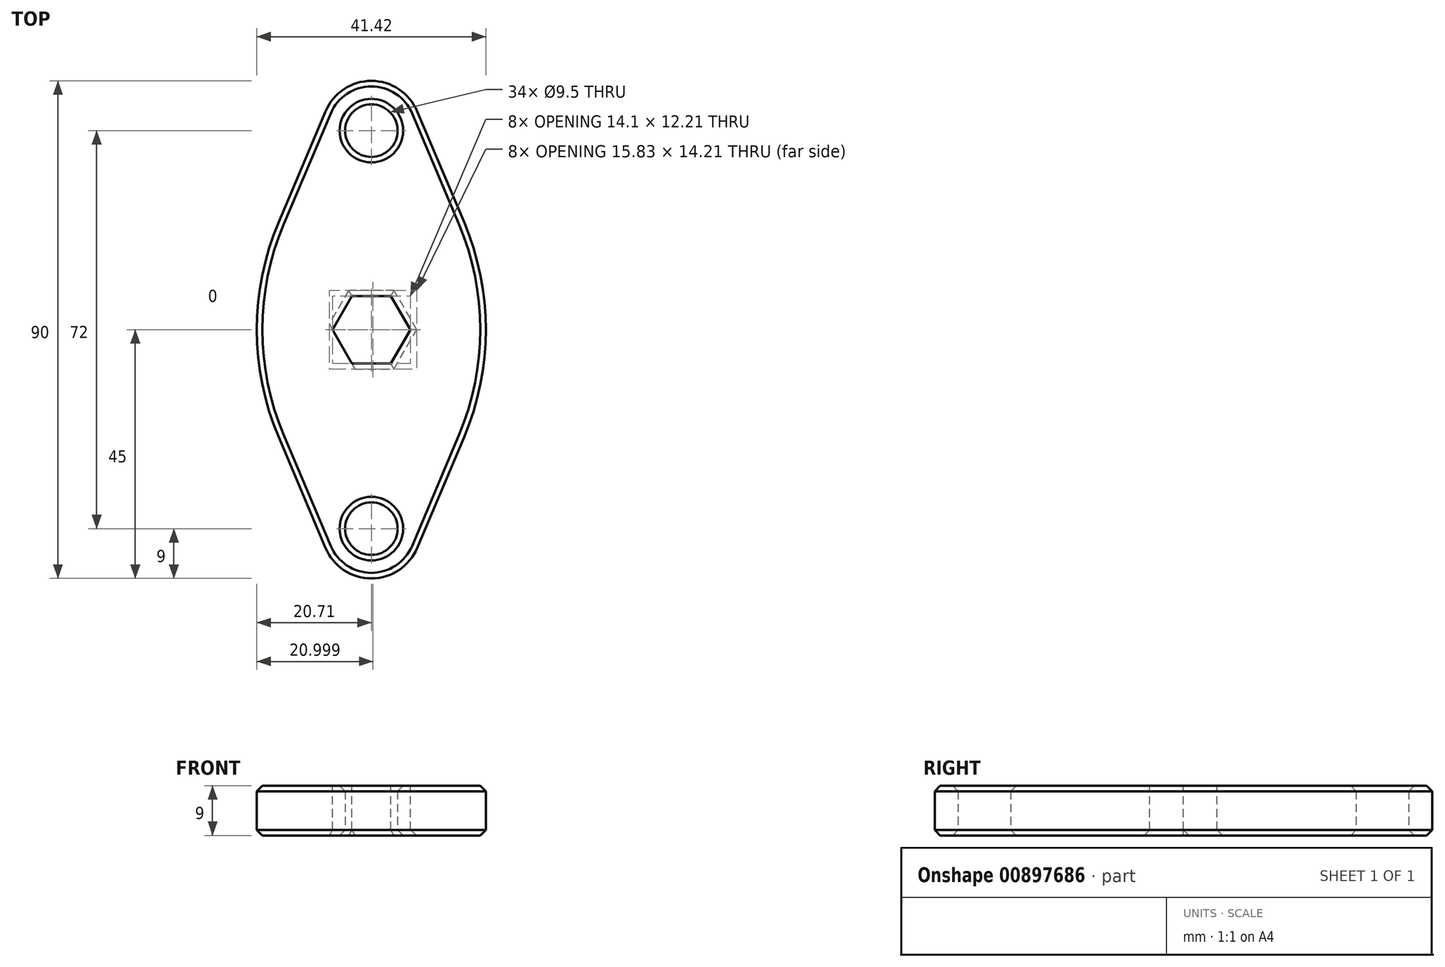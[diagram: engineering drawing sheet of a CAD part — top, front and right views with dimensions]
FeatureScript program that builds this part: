
annotation { "Feature Type Name" : "Feature", "Feature Type Description" : "" }
export const myFeature = defineFeature(function(context is Context, id is Id, definition is map)
    precondition{}
    {
        {
            var Q0;
            Q0=qCreatedBy(makeId("Top.planeOp"),FACE);
            var sketch = newSketch(context, id + "F0", { "sketchPlane" : qUnion([Q0])});
            skLineSegment(sketch, "E0", {"start": v(0, 83.57) * mm, "end": v(0, -89.6) * mm, "construction": true});
            skLineSegment(sketch, "E1", {"start": v(81.05, 0) * mm, "end": v(-79.37, 0) * mm, "construction": true});
            skArc(sketch, "E2", {"start": v(8.29, 39.5) * mm, "mid": v(0, 45) * mm, "end": v(-8.29, 39.5) * mm});
            skLineSegment(sketch, "E3", {"start": v(-26.39, 36) * mm, "end": v(35.06, 36) * mm, "construction": true});
            skArc(sketch, "E4.MirrorCS", {"start": v(8.29, -39.5) * mm, "mid": v(0, -45) * mm, "end": v(-8.29, -39.5) * mm});
            skLineSegment(sketch, "E5", {"start": v(-8.29, 39.5) * mm, "end": v(-25, 0) * mm});
            skLineSegment(sketch, "E6.MirrorCS", {"start": v(8.29, 39.5) * mm, "end": v(25, 0) * mm});
            skPoint(sketch, "E7.orphan", {"position": v(-4.96, 47.37) * mm});
            skPoint(sketch, "E8.orphan", {"position": v(4.96, 47.37) * mm});
            skLineSegment(sketch, "E9.MirrorCS", {"start": v(-8.29, -39.5) * mm, "end": v(-25, 0) * mm});
            skLineSegment(sketch, "E10.MirrorCS", {"start": v(8.29, -39.5) * mm, "end": v(25, 0) * mm});
            skPoint(sketch, "E11.end.orphan", {"position": v(-10, 0) * mm});
            skPoint(sketch, "E11.start.orphan", {"position": v(-9, 36) * mm});
            skPoint(sketch, "E12.end.orphan", {"position": v(10, 0) * mm});
            skPoint(sketch, "E13.orphan", {"position": v(9, 36) * mm});
            skPoint(sketch, "E14.MirrorCS.start.orphan", {"position": v(-9, -36) * mm});
            skPoint(sketch, "E15.orphan", {"position": v(9, -36) * mm});
            skLineSegment(sketch, "E16", {"start": v(-34.58, 46.77) * mm, "end": v(38.96, 46.77) * mm, "construction": true});
            skLineSegment(sketch, "E17.MirrorCS", {"start": v(-34.58, -46.78) * mm, "end": v(38.96, -46.77) * mm, "construction": true});
            skCircle(sketch, "E18", {"center": v(0, 36) * mm, "radius": 11.1 * mm, "construction": true});
            skCircle(sketch, "E19", {"center": v(0, 36) * mm, "radius": 4.75 * mm});
            skCircle(sketch, "E20.MirrorC", {"center": v(0, -36) * mm, "radius": 4.75 * mm});
            skSolve(sketch);
        }
        {
            var Q0;
            Q0=makeQuery(id+"F0.imprint","IMPRINT",FACE,{"disambiguationData":[TD([[makeQuery(id+"F0.imprint","IMPRINT",EDGE,{"derivedFrom":sQuery(id+"F0.wireOp",EDGE,"E2")}),1.0]])]});
            extrude(context, id + "F1", {"entities" : qUnion([Q0]), "endBound" : BoundingType.SYMMETRIC, "depth" : 9 * mm, "offsetDistance" : 25 * mm});
        }
        {
            var Q0;
            Q0=makeQuery(id+"F1.opExtrude","SWEPT_EDGE",EDGE,{"disambiguationData":[OSD([sQuery(id+"F0.wireOp",EDGE,"E5"),sQuery(id+"F0.wireOp",EDGE,"E9.MirrorCS")])]});
            var Q1;
            Q1=makeQuery(id+"F1.opExtrude","SWEPT_EDGE",EDGE,{"disambiguationData":[OSD([sQuery(id+"F0.wireOp",EDGE,"E6.MirrorCS"),sQuery(id+"F0.wireOp",EDGE,"E10.MirrorCS")])]});
            fillet(context, id + "F2", {"entities" : qUnion([Q0, Q1]), "radius" : 50 * mm, "tangentPropagation" : true, "allowEdgeOverflow" : false});
        }
        {
            var Q0;
            Q0=makeQuery(id+"F1.opExtrude","CAP_EDGE",EDGE,{"disambiguationData":[OSD([sQuery(id+"F0.wireOp",EDGE,"E2")])],"isStart":false});
            var Q1;
            Q1=makeQuery(id+"F1.opExtrude","CAP_EDGE",EDGE,{"disambiguationData":[OSD([sQuery(id+"F0.wireOp",EDGE,"E2")])],"isStart":true});
            var Q2;
            Q2=makeQuery(id+"F1.opExtrude","CAP_EDGE",EDGE,{"disambiguationData":[OSD([sQuery(id+"F0.wireOp",EDGE,"E9.MirrorCS")])],"isStart":false});
            var Q3;
            Q3=makeQuery(id+"F1.opExtrude","CAP_EDGE",EDGE,{"disambiguationData":[OSD([sQuery(id+"F0.wireOp",EDGE,"E9.MirrorCS")])],"isStart":true});
            chamfer(context, id + "F3", {"entities" : qUnion([Q0, Q1, Q2, Q3]), "width" : 1 * mm, "tangentPropagation" : true});
        }
        {
            var Q0;
            Q0=makeQuery(id+"F1.opExtrude","CAP_FACE",FACE,{"disambiguationData":[OSD([sQuery(id+"F0.wireOp",EDGE,"E2"),sQuery(id+"F0.wireOp",EDGE,"E4.MirrorCS"),sQuery(id+"F0.wireOp",EDGE,"E5"),sQuery(id+"F0.wireOp",EDGE,"E6.MirrorCS"),sQuery(id+"F0.wireOp",EDGE,"E9.MirrorCS"),sQuery(id+"F0.wireOp",EDGE,"E10.MirrorCS"),sQuery(id+"F0.wireOp",EDGE,"E19"),sQuery(id+"F0.wireOp",EDGE,"E20.MirrorC")])],"isStart":false});
            var sketch = newSketch(context, id + "F4", { "sketchPlane" : qUnion([Q0])});
            skLineSegment(sketch, "E21", {"start": v(-9.19, 0) * mm, "end": v(9.74, 0) * mm, "construction": true});
            skLineSegment(sketch, "E22", {"start": v(0, 0) * mm, "end": v(-4.47, 7.74) * mm, "construction": true});
            skLineSegment(sketch, "E23.MirrorCS", {"start": v(0, 0) * mm, "end": v(4.47, 7.74) * mm, "construction": true});
            skLineSegment(sketch, "E24.MirrorCS", {"start": v(0, 0) * mm, "end": v(-4.47, -7.74) * mm, "construction": true});
            skLineSegment(sketch, "E25.MirrorCS", {"start": v(0, 0) * mm, "end": v(4.47, -7.74) * mm, "construction": true});
            skLineSegment(sketch, "E26", {"start": v(-7.05, 0) * mm, "end": v(-3.53, 6.1) * mm});
            skLineSegment(sketch, "E27", {"start": v(-3.52, 6.1) * mm, "end": v(3.52, 6.1) * mm});
            skLineSegment(sketch, "E28", {"start": v(3.52, 6.1) * mm, "end": v(7.05, 0) * mm});
            skLineSegment(sketch, "E29", {"start": v(7.05, 0) * mm, "end": v(3.52, -6.1) * mm});
            skLineSegment(sketch, "E30", {"start": v(3.52, -6.1) * mm, "end": v(-3.53, -6.1) * mm});
            skLineSegment(sketch, "E31", {"start": v(-3.53, -6.1) * mm, "end": v(-7.05, 0) * mm});
            skSolve(sketch);
        }
        {
            var Q0;
            Q0 = qSketchRegion(id + "F4", true);
            extrude(context, id + "F5", {"entities" : qUnion([Q0]), "operationType" : NewBodyOperationType.REMOVE, "oppositeDirection" : true, "depth" : 25 * mm, "offsetDistance" : 25 * mm});
        }
        {
            var Q0;
            Q0=makeQuery(id+"F1.opExtrude","CAP_EDGE",EDGE,{"disambiguationData":[OSD([sQuery(id+"F0.wireOp",EDGE,"E19")])],"isStart":false});
            var Q1;
            Q1=makeQuery(id+"F1.opExtrude","CAP_EDGE",EDGE,{"disambiguationData":[OSD([sQuery(id+"F0.wireOp",EDGE,"E19")])],"isStart":true});
            var Q2;
            Q2=makeQuery(id+"F1.opExtrude","CAP_EDGE",EDGE,{"disambiguationData":[OSD([sQuery(id+"F0.wireOp",EDGE,"E20.MirrorC")])],"isStart":false});
            var Q3;
            Q3=makeQuery(id+"F1.opExtrude","CAP_EDGE",EDGE,{"disambiguationData":[OSD([sQuery(id+"F0.wireOp",EDGE,"E20.MirrorC")])],"isStart":true});
            var Q4;
            Q4=makeQuery(id+"F5.boolean.opBoolean","COPY",EDGE,{"derivedFrom":makeQuery(id+"F5.opExtrude","CAP_EDGE",EDGE,{"disambiguationData":[OSD([sQuery(id+"F4.wireOp",EDGE,"E30")])],"isStart":true})});
            var Q5;
            Q5=makeQuery(id+"F5.boolean.opBoolean","COPY",EDGE,{"derivedFrom":makeQuery(id+"F5.opExtrude","CAP_EDGE",EDGE,{"disambiguationData":[OSD([sQuery(id+"F4.wireOp",EDGE,"E31")])],"isStart":true})});
            var Q6;
            Q6=makeQuery(id+"F5.boolean.opBoolean","COPY",EDGE,{"derivedFrom":makeQuery(id+"F5.opExtrude","CAP_EDGE",EDGE,{"disambiguationData":[OSD([sQuery(id+"F4.wireOp",EDGE,"E26")])],"isStart":true})});
            var Q7;
            Q7=makeQuery(id+"F5.boolean.opBoolean","COPY",EDGE,{"derivedFrom":makeQuery(id+"F5.opExtrude","CAP_EDGE",EDGE,{"disambiguationData":[OSD([sQuery(id+"F4.wireOp",EDGE,"E27")])],"isStart":true})});
            var Q8;
            Q8=makeQuery(id+"F5.boolean.opBoolean","COPY",EDGE,{"derivedFrom":makeQuery(id+"F5.opExtrude","CAP_EDGE",EDGE,{"disambiguationData":[OSD([sQuery(id+"F4.wireOp",EDGE,"E28")])],"isStart":true})});
            var Q9;
            Q9=makeQuery(id+"F5.boolean.opBoolean","COPY",EDGE,{"derivedFrom":makeQuery(id+"F5.opExtrude","CAP_EDGE",EDGE,{"disambiguationData":[OSD([sQuery(id+"F4.wireOp",EDGE,"E29")])],"isStart":true})});
            var Q10;
            Q10=makeQuery(id+"F5.boolean.opBoolean","INTERSECT",EDGE,{"derivedFrom":[makeQuery(id+"F1.opExtrude","CAP_FACE",FACE,{"disambiguationData":[OSD([sQuery(id+"F0.wireOp",EDGE,"E2"),sQuery(id+"F0.wireOp",EDGE,"E4.MirrorCS"),sQuery(id+"F0.wireOp",EDGE,"E5"),sQuery(id+"F0.wireOp",EDGE,"E6.MirrorCS"),sQuery(id+"F0.wireOp",EDGE,"E9.MirrorCS"),sQuery(id+"F0.wireOp",EDGE,"E10.MirrorCS"),sQuery(id+"F0.wireOp",EDGE,"E19"),sQuery(id+"F0.wireOp",EDGE,"E20.MirrorC")])],"isStart":true}),makeQuery(id+"F5.opExtrude","SWEPT_FACE",FACE,{"disambiguationData":[OSD([sQuery(id+"F4.wireOp",EDGE,"E30")])]})]});
            var Q11;
            Q11=makeQuery(id+"F5.boolean.opBoolean","INTERSECT",EDGE,{"derivedFrom":[makeQuery(id+"F1.opExtrude","CAP_FACE",FACE,{"disambiguationData":[OSD([sQuery(id+"F0.wireOp",EDGE,"E2"),sQuery(id+"F0.wireOp",EDGE,"E4.MirrorCS"),sQuery(id+"F0.wireOp",EDGE,"E5"),sQuery(id+"F0.wireOp",EDGE,"E6.MirrorCS"),sQuery(id+"F0.wireOp",EDGE,"E9.MirrorCS"),sQuery(id+"F0.wireOp",EDGE,"E10.MirrorCS"),sQuery(id+"F0.wireOp",EDGE,"E19"),sQuery(id+"F0.wireOp",EDGE,"E20.MirrorC")])],"isStart":true}),makeQuery(id+"F5.opExtrude","SWEPT_FACE",FACE,{"disambiguationData":[OSD([sQuery(id+"F4.wireOp",EDGE,"E29")])]})]});
            var Q12;
            Q12=makeQuery(id+"F5.boolean.opBoolean","INTERSECT",EDGE,{"derivedFrom":[makeQuery(id+"F1.opExtrude","CAP_FACE",FACE,{"disambiguationData":[OSD([sQuery(id+"F0.wireOp",EDGE,"E2"),sQuery(id+"F0.wireOp",EDGE,"E4.MirrorCS"),sQuery(id+"F0.wireOp",EDGE,"E5"),sQuery(id+"F0.wireOp",EDGE,"E6.MirrorCS"),sQuery(id+"F0.wireOp",EDGE,"E9.MirrorCS"),sQuery(id+"F0.wireOp",EDGE,"E10.MirrorCS"),sQuery(id+"F0.wireOp",EDGE,"E19"),sQuery(id+"F0.wireOp",EDGE,"E20.MirrorC")])],"isStart":true}),makeQuery(id+"F5.opExtrude","SWEPT_FACE",FACE,{"disambiguationData":[OSD([sQuery(id+"F4.wireOp",EDGE,"E28")])]})]});
            var Q13;
            Q13=makeQuery(id+"F5.boolean.opBoolean","INTERSECT",EDGE,{"derivedFrom":[makeQuery(id+"F1.opExtrude","CAP_FACE",FACE,{"disambiguationData":[OSD([sQuery(id+"F0.wireOp",EDGE,"E2"),sQuery(id+"F0.wireOp",EDGE,"E4.MirrorCS"),sQuery(id+"F0.wireOp",EDGE,"E5"),sQuery(id+"F0.wireOp",EDGE,"E6.MirrorCS"),sQuery(id+"F0.wireOp",EDGE,"E9.MirrorCS"),sQuery(id+"F0.wireOp",EDGE,"E10.MirrorCS"),sQuery(id+"F0.wireOp",EDGE,"E19"),sQuery(id+"F0.wireOp",EDGE,"E20.MirrorC")])],"isStart":true}),makeQuery(id+"F5.opExtrude","SWEPT_FACE",FACE,{"disambiguationData":[OSD([sQuery(id+"F4.wireOp",EDGE,"E27")])]})]});
            var Q14;
            Q14=makeQuery(id+"F5.boolean.opBoolean","INTERSECT",EDGE,{"derivedFrom":[makeQuery(id+"F1.opExtrude","CAP_FACE",FACE,{"disambiguationData":[OSD([sQuery(id+"F0.wireOp",EDGE,"E2"),sQuery(id+"F0.wireOp",EDGE,"E4.MirrorCS"),sQuery(id+"F0.wireOp",EDGE,"E5"),sQuery(id+"F0.wireOp",EDGE,"E6.MirrorCS"),sQuery(id+"F0.wireOp",EDGE,"E9.MirrorCS"),sQuery(id+"F0.wireOp",EDGE,"E10.MirrorCS"),sQuery(id+"F0.wireOp",EDGE,"E19"),sQuery(id+"F0.wireOp",EDGE,"E20.MirrorC")])],"isStart":true}),makeQuery(id+"F5.opExtrude","SWEPT_FACE",FACE,{"disambiguationData":[OSD([sQuery(id+"F4.wireOp",EDGE,"E26")])]})]});
            chamfer(context, id + "F6", {"entities" : qUnion([Q0, Q1, Q2, Q3, Q4, Q5, Q6, Q7, Q8, Q9, Q10, Q11, Q12, Q13, Q14]), "width" : 1 * mm, "tangentPropagation" : true});
        }
    });
